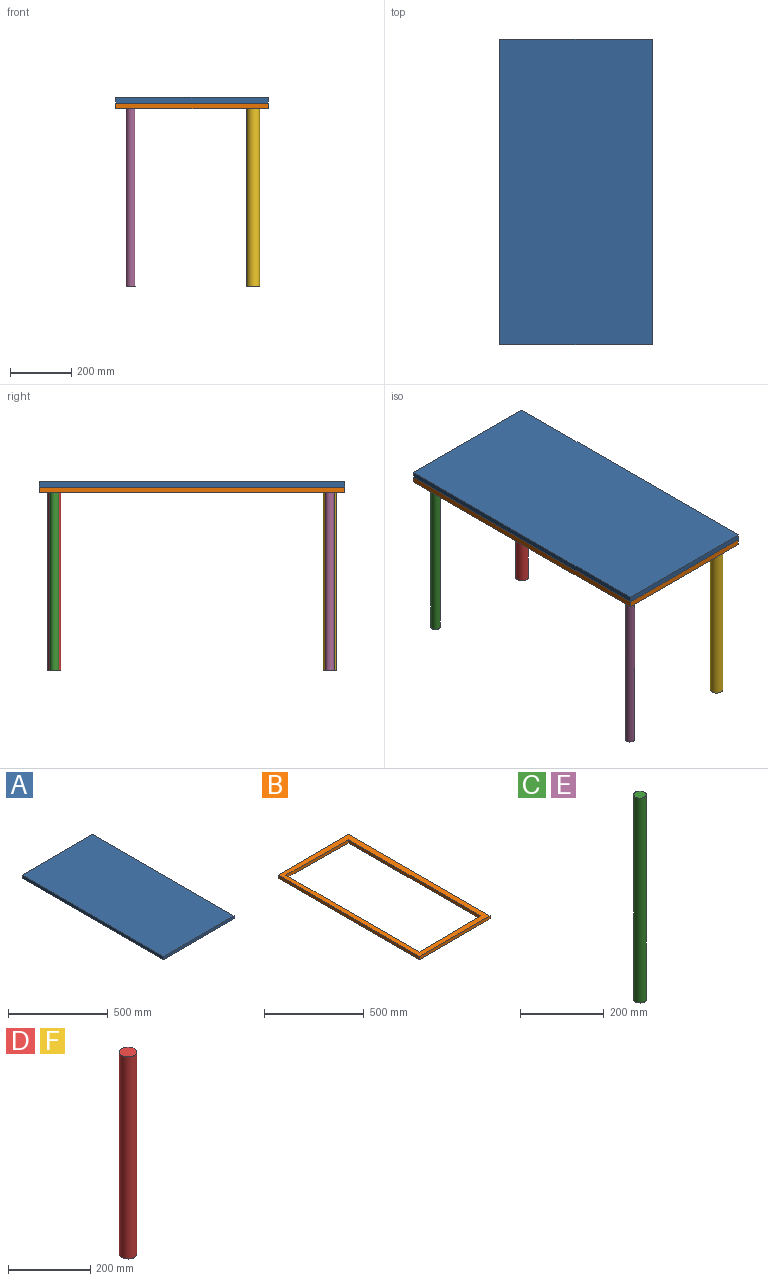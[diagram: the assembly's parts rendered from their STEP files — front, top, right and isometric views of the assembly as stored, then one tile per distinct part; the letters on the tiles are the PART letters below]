
ASSEMBLY  parts=6 mates=5
PART A: 6 faces, bbox 500x1000x19 mm
  f0: plane 1000x19mm, normal (1,0,0), area 19000mm2, adj f1,f3,f4,f5
  f1: plane 500x19mm, normal (0,1,0), area 9500mm2, adj f0,f2,f4,f5
  f2: plane 1000x19mm, normal (-1,0,0), area 19000mm2, adj f1,f3,f4,f5
  f3: plane 500x19mm, normal (0,-1,0), area 9500mm2, adj f0,f2,f4,f5
  f4: plane 1000x500mm, normal (0,0,1), area 500000mm2, adj f0,f1,f2,f3
  f5: plane 1000x500mm, normal (0,0,-1), area 500000mm2, adj f0,f1,f2,f3
PART B: 10 faces, bbox 500x1000x19 mm
  f0: plane 1000x500mm, normal (0,0,1), area 89156mm2, adj f1,f2,f3,f4,f6,f7,f8,f9
  f1: plane 1000x19mm, normal (1,0,0), area 19000mm2, adj f0,f2,f4,f5
  f2: plane 500x19mm, normal (0,1,0), area 9500mm2, adj f0,f1,f3,f5
  f3: plane 1000x19mm, normal (-1,0,0), area 19000mm2, adj f0,f2,f4,f5
  f4: plane 500x19mm, normal (0,-1,0), area 9500mm2, adj f0,f1,f3,f5
  f5: plane 1000x500mm, normal (0,0,-1), area 89156mm2, adj f1,f2,f3,f4,f6,f7,f8,f9
  f6: plane 932x19mm, normal (-1,0,0), area 17708mm2, adj f0,f5,f7,f8
  f7: plane 438x19mm, normal (-0.01,-1,0), area 8322.8mm2, adj f0,f5,f6,f9
  f8: plane 438x19mm, normal (-0.01,1,0), area 8322.8mm2, adj f0,f5,f6,f9
  f9: plane 944x19mm, normal (1,0,0), area 17936mm2, adj f0,f5,f7,f8
PART C: 3 faces, bbox 30x30x600 mm
  f0: cylinder r=15mm len=600mm, axis (0,0,-1), area 56548.7mm2, adj f1,f2
  f1: plane 30x30mm, normal (0,0,1), area 706.9mm2, adj f0
  f2: plane 30x30mm, normal (0,0,-1), area 706.9mm2, adj f0
PART D: 3 faces, bbox 42x42x600 mm
  f0: cylinder r=21mm len=600mm, axis (0,0,-1), area 79168.1mm2, adj f1,f2
  f1: plane 42x42mm, normal (0,0,1), area 1385.4mm2, adj f0
  f2: plane 42x42mm, normal (0,0,-1), area 1385.4mm2, adj f0
PART E: same geometry as C
PART F: same geometry as D
PLACE A rot(axis=(0,0,-1),180deg) t=(252.03,228.98,371.02)mm
PLACE B rot(axis=(0,0,-1),180deg) t=(328.84,164.86,352.02)mm
PLACE C rot(axis=(0,0,-1),180deg) t=(52.03,678.98,-228.98)mm
PLACE D rot(axis=(0,0,-1),180deg) t=(452.03,678.98,-228.98)mm
PLACE E rot(axis=(0,0,-1),180deg) t=(52.03,-221.02,-228.98)mm
PLACE F rot(axis=(0,0,-1),180deg) t=(452.03,-221.02,-228.98)mm
MATE fastened A.f5 <-> C.f1  axis (0,0,-1) through (2.03,728.98,371.02)mm
MATE fastened D.f0 <-> A.f5  axis (0,0,1) through (452.03,678.98,371.02)mm
MATE fastened E.f0 <-> A.f5  axis (0,0,1) through (52.03,-221.02,371.02)mm
MATE fastened B.f0 <-> A.f5  axis (0,0,1) through (502.03,-271.02,371.02)mm
MATE fastened F.f0 <-> A.f5  axis (0,0,1) through (452.03,-221.02,371.02)mm
